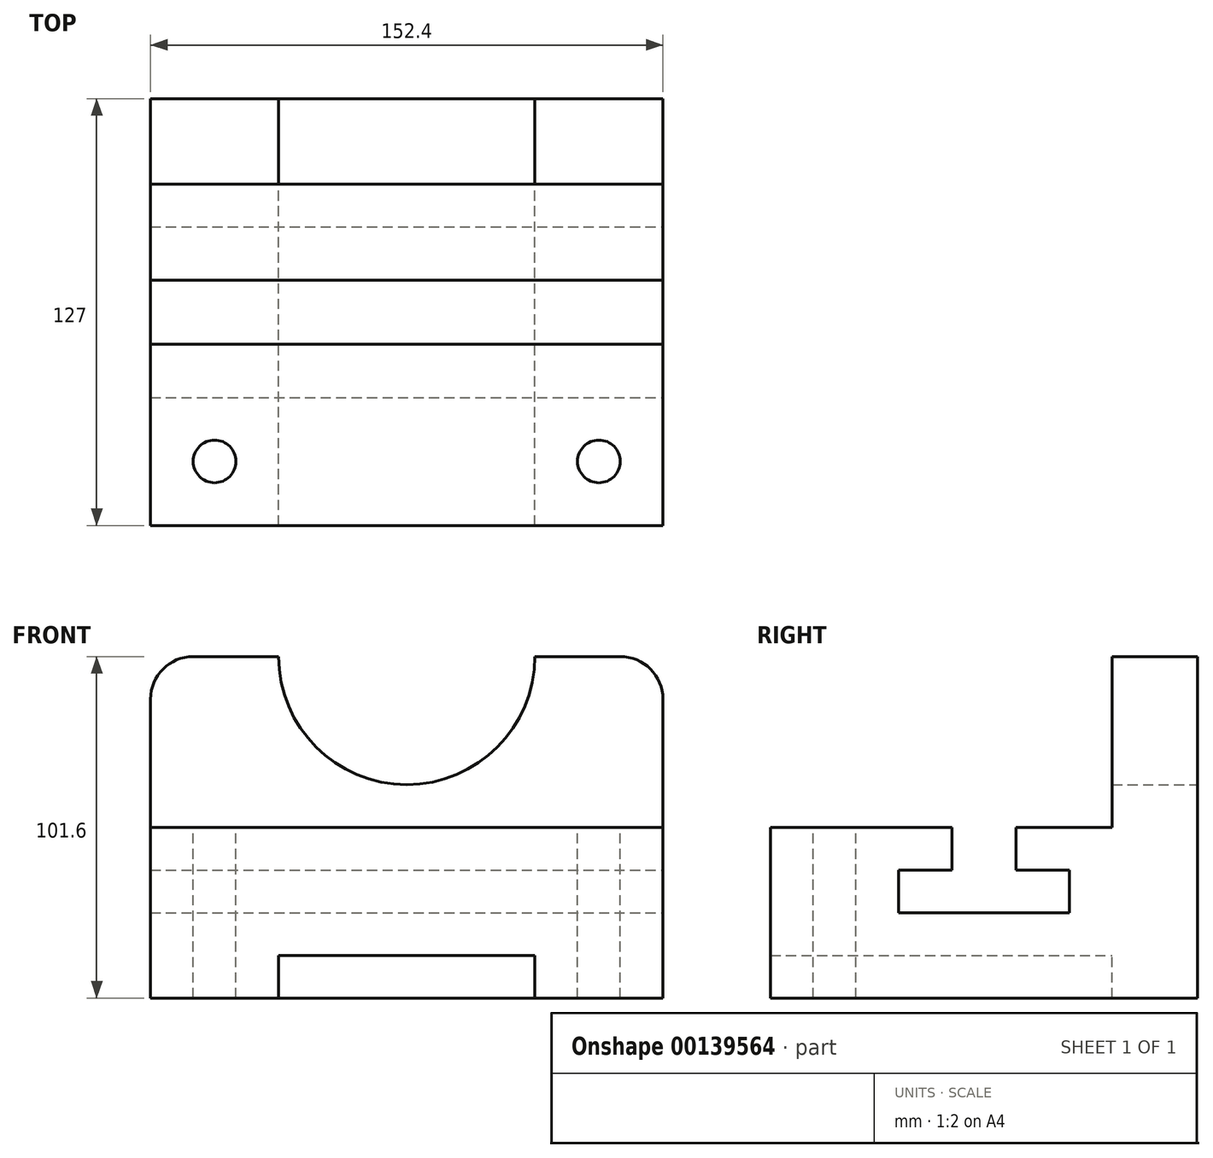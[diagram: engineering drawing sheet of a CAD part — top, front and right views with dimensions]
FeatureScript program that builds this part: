
annotation { "Feature Type Name" : "Feature", "Feature Type Description" : "" }
export const myFeature = defineFeature(function(context is Context, id is Id, definition is map)
    precondition{}
    {
        {
            var Q0;
            Q0=qCreatedBy(makeId("Front.planeOp"),FACE);
            var sketch = newSketch(context, id + "F0", { "sketchPlane" : qUnion([Q0])});
            skLineSegment(sketch, "E0", {"start": v(-76.2, 0) * mm, "end": v(-76.2, 50.8) * mm});
            skLineSegment(sketch, "E1", {"start": v(-76.2, 50.8) * mm, "end": v(76.2, 50.8) * mm});
            skLineSegment(sketch, "E2", {"start": v(76.2, 50.8) * mm, "end": v(76.2, 0) * mm});
            skLineSegment(sketch, "E3", {"start": v(0, 12.7) * mm, "end": v(38.1, 12.7) * mm});
            skLineSegment(sketch, "E4", {"start": v(0, 12.7) * mm, "end": v(-38.1, 12.7) * mm});
            skLineSegment(sketch, "E5", {"start": v(-76.2, 0) * mm, "end": v(-38.1, 0) * mm});
            skLineSegment(sketch, "E6", {"start": v(-38.1, 0) * mm, "end": v(-38.1, 12.7) * mm});
            skLineSegment(sketch, "E7", {"start": v(38.1, 12.7) * mm, "end": v(38.1, 0) * mm});
            skLineSegment(sketch, "E8", {"start": v(38.1, 0) * mm, "end": v(76.2, 0) * mm});
            skSolve(sketch);
        }
        {
            var Q0;
            Q0 = qSketchRegion(id + "F0", true);
            extrude(context, id + "F1", {"entities" : qUnion([Q0]), "endBound" : BoundingType.SYMMETRIC, "depth" : 101.6 * mm});
        }
        {
            var Q0;
            Q0=makeQuery(id+"F1.opExtrude","SWEPT_FACE",FACE,{"disambiguationData":[OSD([sQuery(id+"F0.wireOp",EDGE,"E1")])]});
            var sketch = newSketch(context, id + "F2", { "sketchPlane" : qUnion([Q0])});
            skCircle(sketch, "E9", {"center": v(-57.15, -31.75) * mm, "radius": 6.35 * mm});
            skCircle(sketch, "E10", {"center": v(57.15, -31.75) * mm, "radius": 6.35 * mm});
            skSolve(sketch);
        }
        {
            var Q0;
            Q0 = qSketchRegion(id + "F2", true);
            extrude(context, id + "F3", {"entities" : qUnion([Q0]), "operationType" : NewBodyOperationType.REMOVE, "oppositeDirection" : true, "depth" : 50.8 * mm});
        }
        {
            var Q0;
            Q0=makeQuery(id+"F1.opExtrude","SWEPT_FACE",FACE,{"disambiguationData":[OSD([sQuery(id+"F0.wireOp",EDGE,"E2")])]});
            var sketch = newSketch(context, id + "F4", { "sketchPlane" : qUnion([Q0])});
            skLineSegment(sketch, "E11", {"start": v(-12.7, 25.4) * mm, "end": v(38.1, 25.4) * mm});
            skLineSegment(sketch, "E12", {"start": v(-12.7, 25.4) * mm, "end": v(-12.7, 38.1) * mm});
            skLineSegment(sketch, "E13", {"start": v(-12.7, 38.1) * mm, "end": v(3.17, 38.1) * mm});
            skLineSegment(sketch, "E14", {"start": v(3.17, 38.1) * mm, "end": v(3.17, 50.8) * mm});
            skLineSegment(sketch, "E15", {"start": v(38.1, 25.4) * mm, "end": v(38.1, 38.1) * mm});
            skLineSegment(sketch, "E16", {"start": v(38.1, 38.1) * mm, "end": v(22.23, 38.1) * mm});
            skLineSegment(sketch, "E17", {"start": v(22.23, 38.1) * mm, "end": v(22.22, 50.8) * mm});
            skLineSegment(sketch, "E18", {"start": v(22.22, 50.8) * mm, "end": v(3.17, 50.8) * mm});
            skSolve(sketch);
        }
        {
            var Q0;
            Q0 = qSketchRegion(id + "F4", true);
            extrude(context, id + "F5", {"entities" : qUnion([Q0]), "operationType" : NewBodyOperationType.REMOVE, "oppositeDirection" : true, "depth" : 152.4 * mm});
        }
        {
            var Q0;
            Q0=makeQuery(id+"F1.opExtrude","SWEPT_FACE",FACE,{"disambiguationData":[OSD([sQuery(id+"F0.wireOp",EDGE,"E2")])]});
            var sketch = newSketch(context, id + "F6", { "sketchPlane" : qUnion([Q0])});
            skLineSegment(sketch, "E19", {"start": v(50.8, 50.8) * mm, "end": v(50.8, 0) * mm});
            skLineSegment(sketch, "E20", {"start": v(50.8, 0) * mm, "end": v(76.2, 0) * mm});
            skLineSegment(sketch, "E21", {"start": v(76.2, 0) * mm, "end": v(76.2, 101.6) * mm});
            skLineSegment(sketch, "E22", {"start": v(76.2, 101.6) * mm, "end": v(50.8, 101.6) * mm});
            skLineSegment(sketch, "E23", {"start": v(50.8, 50.8) * mm, "end": v(50.8, 101.6) * mm});
            skSolve(sketch);
        }
        {
            var Q0;
            Q0 = qSketchRegion(id + "F6", true);
            extrude(context, id + "F7", {"entities" : qUnion([Q0]), "operationType" : NewBodyOperationType.ADD, "oppositeDirection" : true, "depth" : 152.4 * mm});
        }
        {
            var Q0;
            Q0=makeQuery(id+"F7.opExtrude","SWEPT_FACE",FACE,{"disambiguationData":[OSD([sQuery(id+"F6.wireOp",EDGE,"E21")])]});
            var sketch = newSketch(context, id + "F8", { "sketchPlane" : qUnion([Q0])});
            skArc(sketch, "E24", {"start": v(-38.1, 101.6) * mm, "mid": v(0, 63.5) * mm, "end": v(38.1, 101.6) * mm});
            skLineSegment(sketch, "E25", {"start": v(38.1, 101.6) * mm, "end": v(-38.1, 101.6) * mm});
            skSolve(sketch);
        }
        {
            var Q0;
            Q0 = qSketchRegion(id + "F8", true);
            extrude(context, id + "F9", {"entities" : qUnion([Q0]), "operationType" : NewBodyOperationType.REMOVE, "oppositeDirection" : true, "depth" : 25.4 * mm});
        }
        {
            var Q0;
            Q0=makeQuery(id+"F7.opExtrude","SWEPT_FACE",FACE,{"disambiguationData":[OSD([sQuery(id+"F6.wireOp",EDGE,"E21")])]});
            var sketch = newSketch(context, id + "F10", { "sketchPlane" : qUnion([Q0])});
            skLineSegment(sketch, "E26.0", {"start": v(76.2, 0) * mm, "end": v(76.2, 88.9) * mm});
            skLineSegment(sketch, "E27.0", {"start": v(63.5, 101.6) * mm, "end": v(38.1, 101.6) * mm});
            skLineSegment(sketch, "E28.0", {"start": v(-38.1, 101.6) * mm, "end": v(-76.2, 101.6) * mm});
            skLineSegment(sketch, "E29.0", {"start": v(-76.2, 0) * mm, "end": v(-76.2, 101.6) * mm});
            skPoint(sketch, "E30.visualSharp", {"position": v(76.2, 101.6) * mm});
            skArc(sketch, "E30.filletArc", {"start": v(76.2, 88.9) * mm, "mid": v(72.48, 97.88) * mm, "end": v(63.5, 101.6) * mm});
            skLineSegment(sketch, "E31", {"start": v(76.2, 88.9) * mm, "end": v(76.2, 101.6) * mm});
            skSolve(sketch);
        }
        {
            var Q0;
            {var subQ0=sQuery(id+"F10.wireOp",EDGE,"E30.filletArc");Q0=makeQuery(id+"F10.imprint","IMPRINT",FACE,{"disambiguationData":[TD([[makeQuery(id+"F10.imprint","IMPRINT",EDGE,{"derivedFrom":subQ0}),-1.0]])]});}
            extrude(context, id + "F11", {"entities" : qUnion([Q0]), "operationType" : NewBodyOperationType.REMOVE, "oppositeDirection" : true, "depth" : 25.4 * mm});
        }
        {
            var Q0;
            Q0=makeQuery(id+"F7.opExtrude","SWEPT_FACE",FACE,{"disambiguationData":[OSD([sQuery(id+"F6.wireOp",EDGE,"E21")])]});
            var sketch = newSketch(context, id + "F12", { "sketchPlane" : qUnion([Q0])});
            skLineSegment(sketch, "E32.0", {"start": v(-38.1, 101.6) * mm, "end": v(-63.5, 101.6) * mm});
            skLineSegment(sketch, "E33.0", {"start": v(-76.2, 0) * mm, "end": v(-76.2, 88.9) * mm});
            skPoint(sketch, "E34.visualSharp", {"position": v(-76.2, 101.6) * mm});
            skArc(sketch, "E34.filletArc", {"start": v(-63.5, 101.6) * mm, "mid": v(-72.48, 97.88) * mm, "end": v(-76.2, 88.9) * mm});
            skLineSegment(sketch, "E35", {"start": v(-63.5, 101.6) * mm, "end": v(-76.2, 101.6) * mm});
            skLineSegment(sketch, "E36", {"start": v(-76.2, 88.9) * mm, "end": v(-76.2, 101.6) * mm});
            skSolve(sketch);
        }
        {
            var Q0;
            Q0=makeQuery(id+"F12.imprint","IMPRINT",FACE,{"disambiguationData":[TD([[makeQuery(id+"F12.imprint","IMPRINT",EDGE,{"derivedFrom":sQuery(id+"F12.wireOp",EDGE,"E34.filletArc")}),-1.0]])]});
            extrude(context, id + "F13", {"entities" : qUnion([Q0]), "operationType" : NewBodyOperationType.REMOVE, "oppositeDirection" : true, "depth" : 25.4 * mm});
        }
    });
